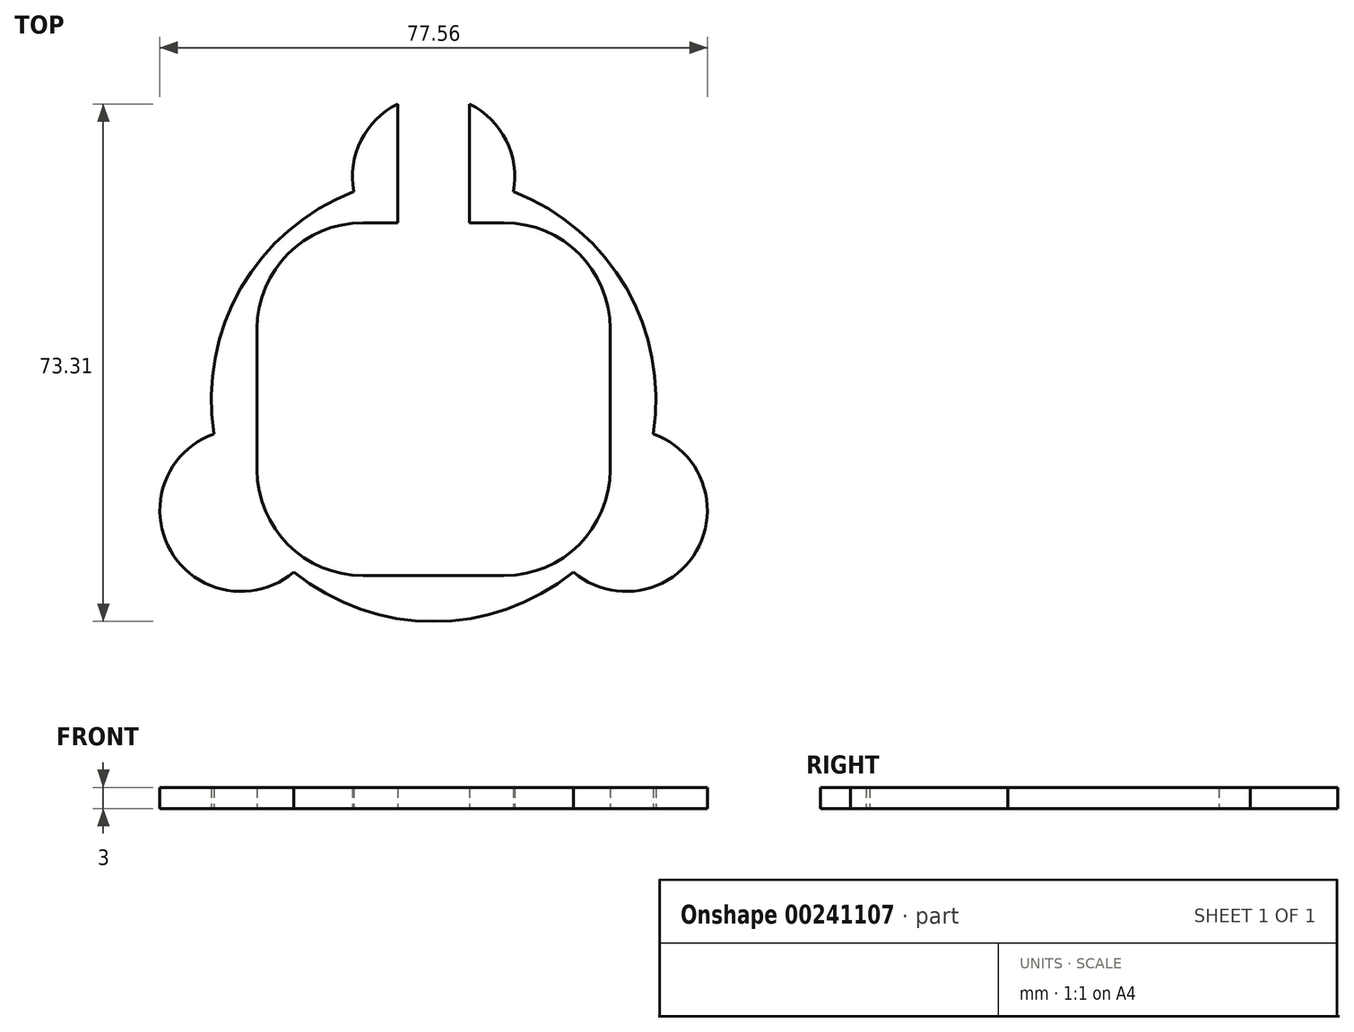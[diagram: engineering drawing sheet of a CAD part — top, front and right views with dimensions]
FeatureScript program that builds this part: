
annotation { "Feature Type Name" : "Feature", "Feature Type Description" : "" }
export const myFeature = defineFeature(function(context is Context, id is Id, definition is map)
    precondition{}
    {
        {
            var Q0;
            Q0=qCreatedBy(makeId("Top.planeOp"),FACE);
            var sketch = newSketch(context, id + "F0", { "sketchPlane" : qUnion([Q0])});
            skPoint(sketch, "E0.center", {"position": v(0, 0) * mm});
            skCircle(sketch, "E1", {"center": v(0, 31.5) * mm, "radius": 11.5 * mm});
            skCircle(sketch, "E2.1.0", {"center": v(-27.28, -15.75) * mm, "radius": 11.5 * mm});
            skCircle(sketch, "E2.2.0", {"center": v(27.28, -15.75) * mm, "radius": 11.5 * mm});
            skCircle(sketch, "E3", {"center": v(0, 0) * mm, "radius": 31.5 * mm});
            skSolve(sketch);
        }
        {
            var Q0;
            Q0=qCreatedBy(makeId("Top.planeOp"),FACE);
            var sketch = newSketch(context, id + "F1", { "sketchPlane" : qUnion([Q0])});
            skLineSegment(sketch, "E4.bottom", {"start": v(5.1, 16.8) * mm, "end": v(-5.1, 16.8) * mm});
            skLineSegment(sketch, "E4.top", {"start": v(5.1, 46.27) * mm, "end": v(-5.1, 46.27) * mm});
            skLineSegment(sketch, "E4.left", {"start": v(5.1, 16.8) * mm, "end": v(5.1, 46.27) * mm});
            skLineSegment(sketch, "E4.right", {"start": v(-5.1, 16.8) * mm, "end": v(-5.1, 46.27) * mm});
            skPoint(sketch, "E4.middle", {"position": v(0, 31.54) * mm});
            skLineSegment(sketch, "E5.bottom", {"start": v(10, -25) * mm, "end": v(-10, -25) * mm});
            skLineSegment(sketch, "E5.top", {"start": v(10, 25) * mm, "end": v(-10, 25) * mm});
            skLineSegment(sketch, "E5.left", {"start": v(25, -10) * mm, "end": v(25, 10) * mm});
            skLineSegment(sketch, "E5.right", {"start": v(-25, -10) * mm, "end": v(-25, 10) * mm});
            skPoint(sketch, "E5.middle", {"position": v(0, 0) * mm});
            skPoint(sketch, "E6.visualSharp", {"position": v(-25, 25) * mm});
            skArc(sketch, "E6.filletArc", {"start": v(-10, 25) * mm, "mid": v(-20.6, 20.6) * mm, "end": v(-25, 10) * mm});
            skPoint(sketch, "E7.visualSharp", {"position": v(25, 25) * mm});
            skArc(sketch, "E7.filletArc", {"start": v(25, 10) * mm, "mid": v(20.6, 20.6) * mm, "end": v(10, 25) * mm});
            skPoint(sketch, "E8.visualSharp", {"position": v(25, -25) * mm});
            skArc(sketch, "E8.filletArc", {"start": v(10, -25) * mm, "mid": v(20.6, -20.6) * mm, "end": v(25, -10) * mm});
            skPoint(sketch, "E9.visualSharp", {"position": v(-25, -25) * mm});
            skArc(sketch, "E9.filletArc", {"start": v(-25, -10) * mm, "mid": v(-20.6, -20.6) * mm, "end": v(-10, -25) * mm});
            skSolve(sketch);
        }
        {
            var Q0;
            Q0=qSketchRegion(id+"F0",true);
            extrude(context, id + "F2", {"entities" : qUnion([Q0]), "depth" : 3 * mm});
        }
        {
            var Q0;
            Q0=qSketchRegion(id+"F1",true);
            extrude(context, id + "F3", {"entities" : qUnion([Q0]), "operationType" : NewBodyOperationType.REMOVE, "depth" : 3 * mm});
        }
    });
